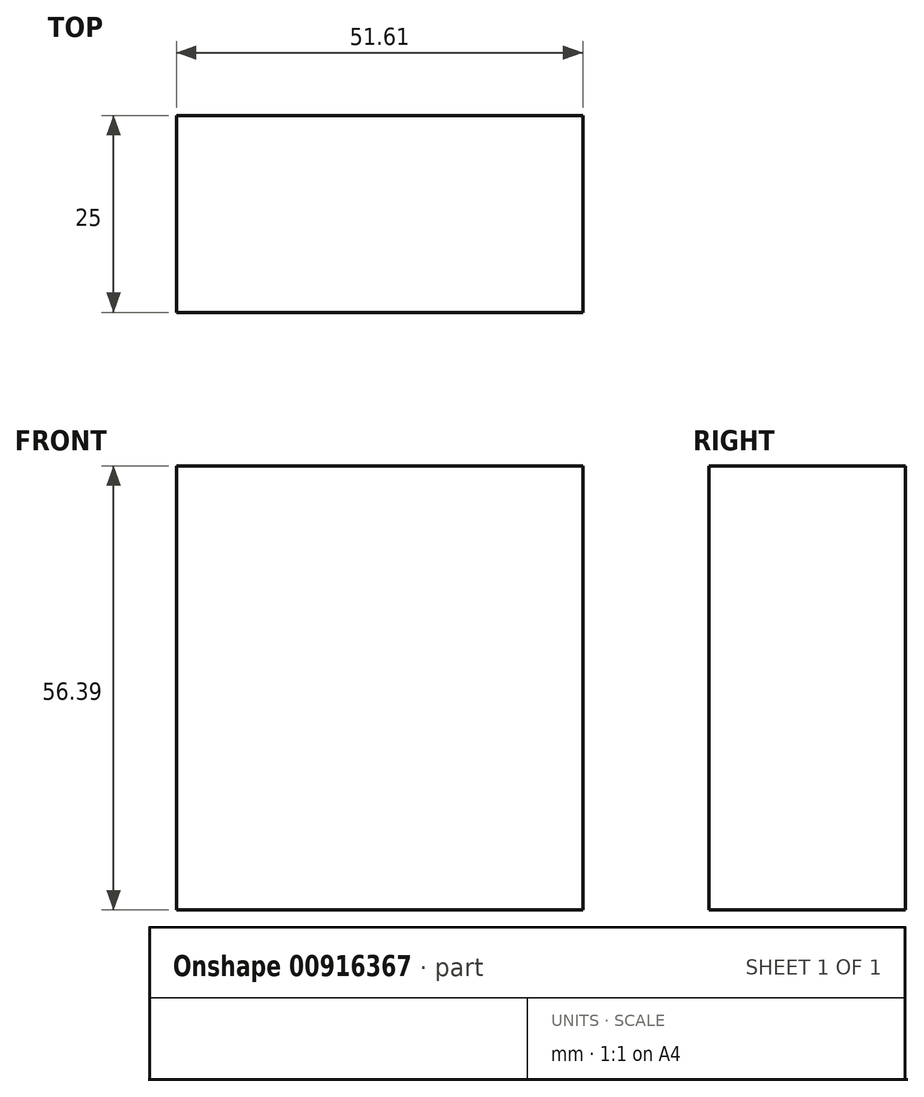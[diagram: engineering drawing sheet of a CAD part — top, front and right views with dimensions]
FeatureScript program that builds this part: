
annotation { "Feature Type Name" : "Feature", "Feature Type Description" : "" }
export const myFeature = defineFeature(function(context is Context, id is Id, definition is map)
    precondition{}
    {
        {
            var Q0;
            Q0=qCreatedBy(makeId("Front.planeOp"),FACE);
            var sketch = newSketch(context, id + "F0", { "sketchPlane" : qUnion([Q0])});
            skLineSegment(sketch, "E0.bottom", {"start": v(-119.33, 29) * mm, "end": v(-67.72, 29) * mm});
            skLineSegment(sketch, "E0.top", {"start": v(-119.33, -27.4) * mm, "end": v(-67.72, -27.4) * mm});
            skLineSegment(sketch, "E0.left", {"start": v(-119.33, 29) * mm, "end": v(-119.33, -27.4) * mm});
            skLineSegment(sketch, "E0.right", {"start": v(-67.72, 29) * mm, "end": v(-67.72, -27.4) * mm});
            skSolve(sketch);
        }
        {
            var Q0;
            Q0 = qSketchRegion(id + "F0", true);
            extrude(context, id + "F1", {"entities" : qUnion([Q0]), "depth" : 25 * mm, "offsetDistance" : 25 * mm});
        }
    });
